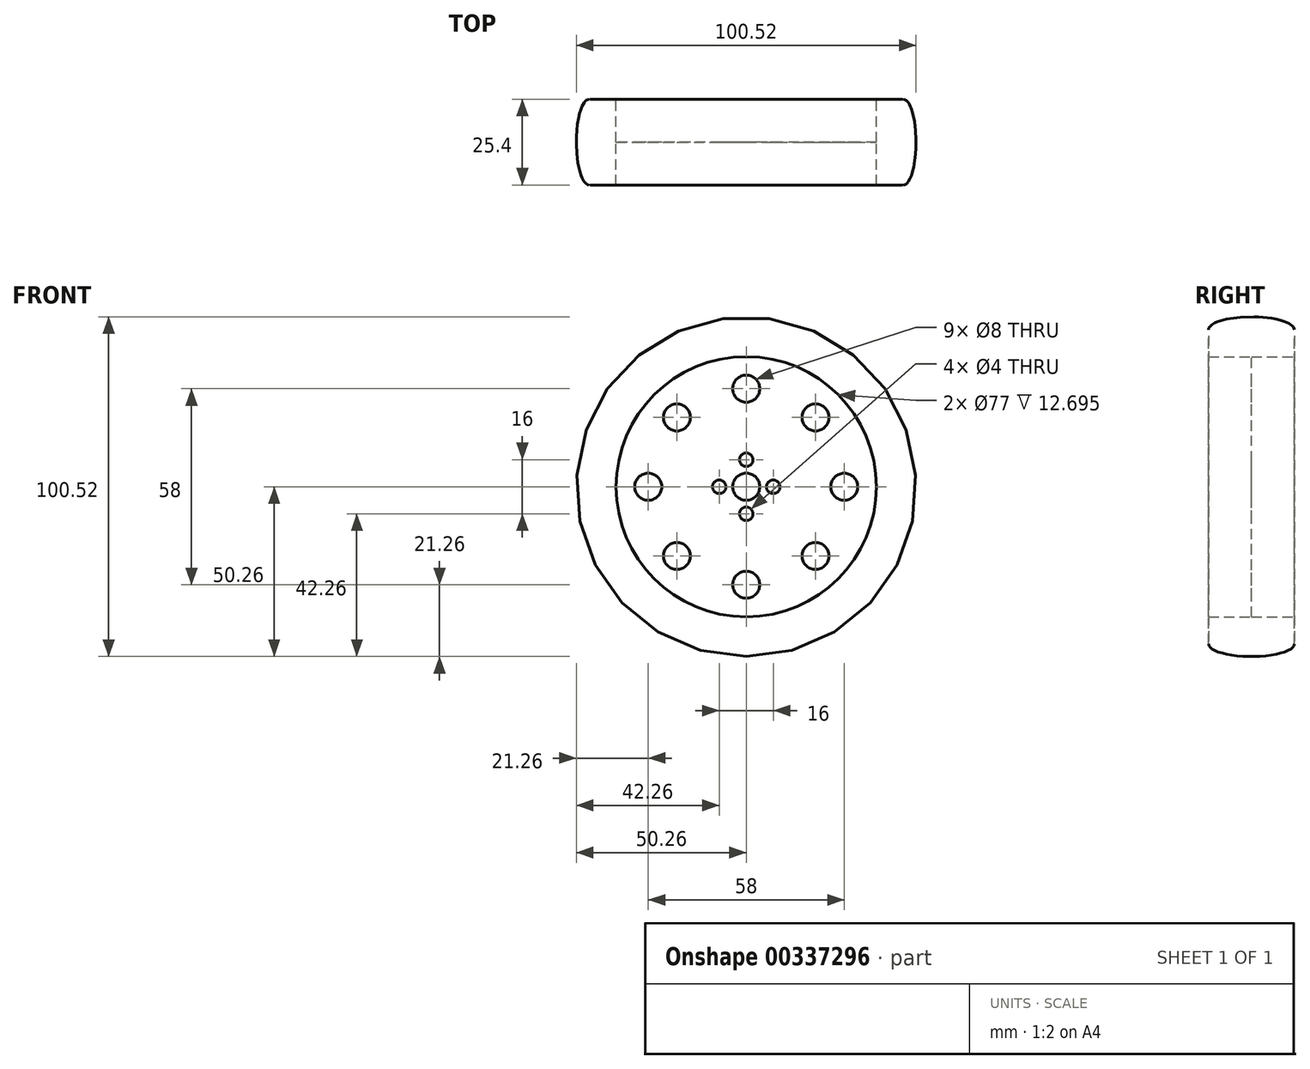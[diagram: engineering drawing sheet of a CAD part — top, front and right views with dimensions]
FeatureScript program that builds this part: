
annotation { "Feature Type Name" : "Feature", "Feature Type Description" : "" }
export const myFeature = defineFeature(function(context is Context, id is Id, definition is map)
    precondition{}
    {
        {
            var Q0;
            Q0=qCreatedBy(makeId("Right.planeOp"),FACE);
            var sketch = newSketch(context, id + "F0", { "sketchPlane" : qUnion([Q0])});
            skLineSegment(sketch, "E0.bottom", {"start": v(12.7, 46.5) * mm, "end": v(-12.7, 46.5) * mm});
            skLineSegment(sketch, "E0.top", {"start": v(12.7, -46.5) * mm, "end": v(-12.7, -46.5) * mm});
            skLineSegment(sketch, "E0.left", {"start": v(12.7, 46.5) * mm, "end": v(12.7, -46.5) * mm});
            skLineSegment(sketch, "E0.right", {"start": v(-12.7, 46.5) * mm, "end": v(-12.7, -46.5) * mm});
            skPoint(sketch, "E0.middle", {"position": v(0, 0) * mm});
            skEllipse(sketch, "E1", {"center": v(0, 46.5) * mm, "majorRadius": 12.7 * mm, "minorRadius": 3.76 * mm, "majorAxis": v(1, 0)});
            skLineSegment(sketch, "E2", {"start": v(-12.7, 0) * mm, "end": v(12.7, 0) * mm});
            skSolve(sketch);
        }
        {
            var Q0;
            {var subQ0=sQuery(id+"F0.wireOp",EDGE,"E0.bottom");Q0=makeQuery(id+"F0.imprint","IMPRINT",FACE,{"disambiguationData":[TD([[makeQuery(id+"F0.imprint","IMPRINT",EDGE,{"derivedFrom":subQ0}),-1.0]])]});}
            var Q1;
            Q1=sQuery(id+"F0.wireOp",EDGE,"E2");
            revolve(context, id + "F1", {"entities" : qUnion([Q0]), "axis" : qUnion([Q1]), "revolveType" : RevolveType.FULL});
        }
        {
            var Q0;
            Q0=qCreatedBy(makeId("Front.planeOp"),FACE);
            var sketch = newSketch(context, id + "F2", { "sketchPlane" : qUnion([Q0])});
            skCircle(sketch, "E3", {"center": v(0, 0) * mm, "radius": 46.5 * mm});
            skCircle(sketch, "E4", {"center": v(0, 29) * mm, "radius": 4 * mm});
            skCircle(sketch, "E5", {"center": v(29, 0) * mm, "radius": 4 * mm});
            skCircle(sketch, "E6", {"center": v(0, 0) * mm, "radius": 4 * mm});
            skCircle(sketch, "E7", {"center": v(0, 8) * mm, "radius": 2 * mm});
            skCircle(sketch, "E8", {"center": v(8, 0) * mm, "radius": 2 * mm});
            skCircle(sketch, "E9", {"center": v(20.5, 20.5) * mm, "radius": 4 * mm});
            skCircle(sketch, "E10.MirrorC", {"center": v(-20.5, 20.5) * mm, "radius": 4 * mm});
            skCircle(sketch, "E11.MirrorC", {"center": v(0, -29) * mm, "radius": 4 * mm});
            skCircle(sketch, "E12.MirrorC", {"center": v(-29, 0) * mm, "radius": 4 * mm});
            skCircle(sketch, "E13.MirrorC", {"center": v(-20.5, -20.5) * mm, "radius": 4 * mm});
            skCircle(sketch, "E14.MirrorC", {"center": v(20.5, -20.5) * mm, "radius": 4 * mm});
            skCircle(sketch, "E15.MirrorC", {"center": v(0, -8) * mm, "radius": 2 * mm});
            skCircle(sketch, "E16.MirrorC", {"center": v(-8, 0) * mm, "radius": 2 * mm});
            skCircle(sketch, "E17", {"center": v(0, 0) * mm, "radius": 38.5 * mm});
            skSolve(sketch);
        }
        {
            var Q0;
            Q0=makeQuery(id+"F2.imprint","IMPRINT",FACE,{"disambiguationData":[TD([[makeQuery(id+"F2.imprint","IMPRINT",EDGE,{"derivedFrom":sQuery(id+"F2.wireOp",EDGE,"E3")}),1.0]])]});
            extrude(context, id + "F3", {"entities" : qUnion([Q0]), "operationType" : NewBodyOperationType.ADD, "endBound" : BoundingType.SYMMETRIC, "depth" : 25.4 * mm});
        }
        {
            var Q0;
            Q0=makeQuery(id+"F2.imprint","IMPRINT",FACE,{"disambiguationData":[TD([[makeQuery(id+"F2.imprint","IMPRINT",EDGE,{"derivedFrom":sQuery(id+"F2.wireOp",EDGE,"E4")}),-1.0]])]});
            extrude(context, id + "F4", {"entities" : qUnion([Q0]), "operationType" : NewBodyOperationType.ADD, "endBound" : BoundingType.SYMMETRIC, "depth" : 4 / 406.4 * mm});
        }
    });
